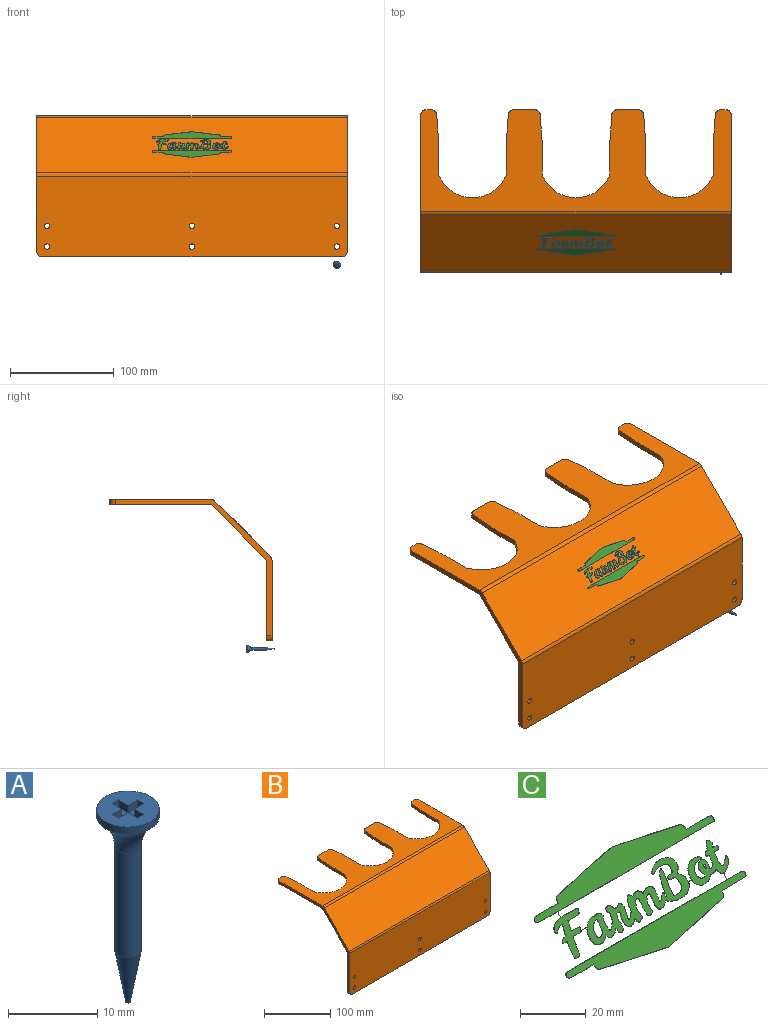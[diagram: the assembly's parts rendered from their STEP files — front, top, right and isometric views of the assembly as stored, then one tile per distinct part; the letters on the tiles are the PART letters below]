
ASSEMBLY  parts=3 mates=1
PART A: 19 faces, bbox 14.1x14.1x26.4 mm
  f0: plane 7x7mm, normal (0,0,1), area 31.5mm2, adj f3,f5,f6,f7,f8,f9,f10,f11
  f1: cylinder r=1.5mm len=14.31mm, axis (0,0,-1), area 134.9mm2, adj f4,f18
  f2: plane 0.5x0.5mm, normal (0,0,-1), area 0.2mm2, adj f18
  f3: cylinder r=3.5mm len=7mm, axis (0,0,-1), area 22mm2, adj f0,f4
  f4: torus R=6.5mm, axis (0,0,1), area 63.7mm2, adj f1,f3
  f5: plane 1.5x1mm, normal (0,1,0), area 1.5mm2, adj f0,f6,f16,f17
  f6: plane 1.5x1mm, normal (1,0,0), area 1.5mm2, adj f0,f5,f7,f17
  f7: plane 1x1mm, normal (0,1,0), area 1mm2, adj f0,f6,f8,f17
  f8: plane 1.5x1mm, normal (-1,0,0), area 1.5mm2, adj f0,f7,f9,f17
  f9: plane 1.5x1mm, normal (0,1,0), area 1.5mm2, adj f0,f8,f10,f17
  f10: plane 1x1mm, normal (-1,0,0), area 1mm2, adj f0,f9,f11,f17
  f11: plane 1.5x1mm, normal (0,-1,0), area 1.5mm2, adj f0,f10,f12,f17
  f12: plane 1.5x1mm, normal (-1,0,0), area 1.5mm2, adj f0,f11,f13,f17
  f13: plane 1x1mm, normal (0,-1,0), area 1mm2, adj f0,f12,f14,f17
  f14: plane 1.5x1mm, normal (1,0,0), area 1.5mm2, adj f0,f13,f15,f17
  f15: plane 1.5x1mm, normal (0,-1,0), area 1.5mm2, adj f0,f14,f16,f17
  f16: plane 1x1mm, normal (1,0,0), area 1mm2, adj f0,f5,f15,f17
  f17: plane 4x4mm, normal (0,0,1), area 7mm2, adj f5,f6,f7,f8,f9,f10,f11,f12
  f18: cone r=1.5mm half-angle=10deg, axis (0,0,1), area 39.6mm2, adj f1,f2
PART B: 52 faces, bbox 300x156.6x136.6 mm
  f0: plane 300x97.93mm, normal (0,0,-1), area 13697.5mm2, adj f1,f3,f4,f5,f6,f7,f8,f9
  f1: plane 5.36x5mm, normal (0,1,0), area 26.8mm2, adj f0,f2,f33,f44
  f2: plane 300x97.93mm, normal (0,0,1), area 13697.5mm2, adj f1,f3,f4,f5,f6,f7,f8,f9
  f3: plane 20.73x5mm, normal (0,1,0), area 103.6mm2, adj f0,f2,f24,f34
  f4: plane 20.73x5mm, normal (0,1,0), area 103.6mm2, adj f0,f2,f15,f25
  f5: plane 5.36x5mm, normal (0,1,0), area 26.8mm2, adj f0,f2,f16,f43
  f6: plane 151.57x131.57mm, normal (-1,0,0), area 1228.2mm2, adj f0,f2,f35,f36,f37,f38,f40,f41
  f7: plane 151.57x131.57mm, normal (1,0,0), area 1228.2mm2, adj f0,f2,f35,f36,f37,f38,f40,f42
  f8: plane 20.82x5mm, normal (-1,0.08,0), area 104.4mm2, adj f0,f2,f14,f15
  f9: plane 20.82x5mm, normal (1,0.08,0), area 104.4mm2, adj f0,f2,f13,f16
  f10: plane 22.43x5mm, normal (1,0,0), area 112.2mm2, adj f0,f2,f11,f13
  f11: cylinder r=35mm len=65mm, axis (0,0,1), area 416.7mm2, adj f0,f2,f10,f12
  f12: plane 22.43x5mm, normal (-1,0,0), area 112.2mm2, adj f0,f2,f11,f14
  f13: cylinder r=200mm len=15.11mm, axis (0,0,1), area 75.6mm2, adj f0,f2,f9,f10
  f14: cylinder r=200mm len=15.11mm, axis (0,0,1), area 75.6mm2, adj f0,f2,f8,f12
  f15: cylinder r=5mm len=5mm, axis (0,0,1), area 37.4mm2, adj f0,f2,f4,f8
  f16: cylinder r=5mm len=5mm, axis (0,0,-1), area 37.4mm2, adj f0,f2,f5,f9
  f17: plane 20.82x5mm, normal (-1,0.08,0), area 104.4mm2, adj f0,f2,f23,f24
  f18: plane 20.82x5mm, normal (1,0.08,0), area 104.4mm2, adj f0,f2,f22,f25
  f19: plane 22.43x5mm, normal (1,0,0), area 112.2mm2, adj f0,f2,f20,f22
  f20: cylinder r=35mm len=65mm, axis (0,0,1), area 416.7mm2, adj f0,f2,f19,f21
  f21: plane 22.43x5mm, normal (-1,0,0), area 112.2mm2, adj f0,f2,f20,f23
  f22: cylinder r=200mm len=15.11mm, axis (0,0,1), area 75.6mm2, adj f0,f2,f18,f19
  f23: cylinder r=200mm len=15.11mm, axis (0,0,1), area 75.6mm2, adj f0,f2,f17,f21
  f24: cylinder r=5mm len=5mm, axis (0,0,1), area 37.4mm2, adj f0,f2,f3,f17
  f25: cylinder r=5mm len=5mm, axis (0,0,-1), area 37.4mm2, adj f0,f2,f4,f18
  f26: plane 20.82x5mm, normal (-1,0.08,0), area 104.4mm2, adj f0,f2,f32,f33
  f27: plane 20.82x5mm, normal (1,0.08,0), area 104.4mm2, adj f0,f2,f31,f34
  f28: plane 22.43x5mm, normal (1,0,0), area 112.2mm2, adj f0,f2,f29,f31
  f29: cylinder r=35mm len=65mm, axis (0,0,1), area 416.7mm2, adj f0,f2,f28,f30
  f30: plane 22.43x5mm, normal (-1,0,0), area 112.2mm2, adj f0,f2,f29,f32
  f31: cylinder r=200mm len=15.11mm, axis (0,0,1), area 75.6mm2, adj f0,f2,f27,f28
  f32: cylinder r=200mm len=15.11mm, axis (0,0,1), area 75.6mm2, adj f0,f2,f26,f30
  f33: cylinder r=5mm len=5mm, axis (0,0,1), area 37.4mm2, adj f0,f1,f2,f26
  f34: cylinder r=5mm len=5mm, axis (0,0,-1), area 37.4mm2, adj f0,f2,f3,f27
  f35: plane 300x53.64mm, normal (0,0.71,-0.71), area 22757.4mm2, adj f0,f6,f7,f37
  f36: plane 300x53.64mm, normal (0,-0.71,0.71), area 22757.4mm2, adj f6,f7,f40,f45
  f37: plane 300x77.93mm, normal (0,1,0), area 23238.1mm2, adj f6,f7,f35,f39,f41,f42,f46,f47
  f38: plane 300x77.93mm, normal (0,-1,0), area 23238.1mm2, adj f6,f7,f39,f40,f41,f42,f46,f47
  f39: plane 290x5mm, normal (0,0,-1), area 1450mm2, adj f37,f38,f41,f42
  f40: cylinder r=5mm len=300mm, axis (1,0,0), area 1178.1mm2, adj f6,f7,f36,f38
  f41: cylinder r=5mm len=5mm, axis (0,1,0), area 39.3mm2, adj f6,f37,f38,f39
  f42: cylinder r=5mm len=5mm, axis (0,-1,0), area 39.3mm2, adj f7,f37,f38,f39
  f43: cylinder r=5mm len=5mm, axis (0,0,-1), area 39.3mm2, adj f0,f2,f5,f6
  f44: cylinder r=5mm len=5mm, axis (0,0,1), area 39.3mm2, adj f0,f1,f2,f7
  f45: cylinder r=5mm len=300mm, axis (1,0,0), area 1178.1mm2, adj f2,f6,f7,f36
  f46: cylinder r=2.62mm len=5.25mm, axis (0,-1,0), area 82.5mm2, adj f37,f38
  f47: cylinder r=2.62mm len=5.25mm, axis (0,-1,0), area 82.5mm2, adj f37,f38
  f48: cylinder r=2.62mm len=5.25mm, axis (0,-1,0), area 82.5mm2, adj f37,f38
  f49: cylinder r=2.62mm len=5.25mm, axis (0,-1,0), area 82.5mm2, adj f37,f38
  f50: cylinder r=2.62mm len=5.25mm, axis (0,-1,0), area 82.5mm2, adj f37,f38
  f51: cylinder r=2.62mm len=5.25mm, axis (0,-1,0), area 82.5mm2, adj f37,f38
PART C: 232 faces, bbox 77x24.9x24.9 mm
  f0: extruded ~0.63x0.63mm, area 0.1mm2, adj f1,f229,f230,f231
  f1: extruded ~0.72x0.72mm, area 0.1mm2, adj f0,f2,f230,f231
  f2: extruded ~0.56x0.56mm, area 0.1mm2, adj f1,f229,f230,f231
  f3: extruded ~1.22x0.3mm, area 0.1mm2, adj f4,f227,f230,f231
  f4: extruded ~0.97x0.97mm, area 0.1mm2, adj f3,f5,f230,f231
  f5: extruded ~2.07x2.07mm, area 0.3mm2, adj f4,f6,f230,f231
  f6: extruded ~1.87x0.7mm, area 0.2mm2, adj f5,f7,f230,f231
  f7: extruded ~0.65x0.65mm, area 0.1mm2, adj f6,f8,f230,f231
  f8: extruded ~1.21x1.21mm, area 0.2mm2, adj f7,f227,f230,f231
  f9: extruded ~6.37x0.14mm, area 0.6mm2, adj f10,f228,f230,f231
  f10: plane 1.72x1.72mm, normal (1,0,0), area 0.2mm2, adj f9,f11,f230,f231
  f11: extruded ~4.13x2.15mm, area 0.5mm2, adj f10,f12,f230,f231
  f12: extruded ~0.88x0.88mm, area 0.1mm2, adj f11,f13,f230,f231
  f13: extruded ~0.93x0.6mm, area 0.1mm2, adj f12,f14,f230,f231
  f14: extruded ~2.2x1mm, area 0.3mm2, adj f13,f15,f230,f231
  f15: extruded ~2.1x2.1mm, area 0.3mm2, adj f14,f16,f230,f231
  f16: extruded ~1.29x1.29mm, area 0.2mm2, adj f15,f17,f230,f231
  f17: extruded ~1.02x0.2mm, area 0.1mm2, adj f16,f18,f230,f231
  f18: extruded ~1.09x0.36mm, area 0.1mm2, adj f17,f19,f230,f231
  f19: extruded ~0.58x0.58mm, area 0.1mm2, adj f18,f20,f230,f231
  f20: extruded ~0.91x0.29mm, area 0.1mm2, adj f19,f21,f230,f231
  f21: extruded ~0.91x0.14mm, area 0.1mm2, adj f20,f22,f230,f231
  f22: extruded ~0.54x0.54mm, area 0.1mm2, adj f21,f23,f230,f231
  f23: plane 0.47x0.47mm, normal (0.87,-0.35,-0.35), area 0.1mm2, adj f22,f24,f230,f231
  f24: plane 0.48x0.48mm, normal (0.91,0.29,0.29), area 0.1mm2, adj f23,f25,f230,f231
  f25: extruded ~2.37x1.45mm, area 0.4mm2, adj f24,f26,f230,f231
  f26: extruded ~0.75x0.6mm, area 0.1mm2, adj f25,f27,f230,f231
  f27: extruded ~0.87x0.75mm, area 0.1mm2, adj f26,f28,f230,f231
  f28: extruded ~0.41x0.4mm, area 0.1mm2, adj f27,f29,f230,f231
  f29: extruded ~0.51x0.12mm, area 0.1mm2, adj f28,f30,f230,f231
  f30: extruded ~0.74x0.74mm, area 0.1mm2, adj f29,f31,f230,f231
  f31: extruded ~1.02x1.02mm, area 0.1mm2, adj f30,f32,f230,f231
  f32: extruded ~1.01x0.93mm, area 0.2mm2, adj f31,f33,f230,f231
  f33: extruded ~0.78x0.28mm, area 0.1mm2, adj f32,f34,f230,f231
  f34: extruded ~0.97x0.97mm, area 0.1mm2, adj f33,f35,f230,f231
  f35: extruded ~1.06x1.06mm, area 0.1mm2, adj f34,f36,f230,f231
  f36: extruded ~1.45x0.55mm, area 0.2mm2, adj f35,f37,f230,f231
  f37: extruded ~3.02x3.02mm, area 0.6mm2, adj f36,f38,f230,f231
  f38: plane 0.45x0.42mm, normal (-0.74,-0.47,-0.47), area 0.1mm2, adj f37,f39,f230,f231
  f39: plane 0.5x0.17mm, normal (-0.27,0.68,0.68), area 0.1mm2, adj f38,f40,f230,f231
  f40: extruded ~2.56x1.49mm, area 0.4mm2, adj f39,f41,f230,f231
  f41: extruded ~2.21x2.21mm, area 0.4mm2, adj f40,f42,f230,f231
  f42: extruded ~1.46x0.26mm, area 0.1mm2, adj f41,f43,f230,f231
  f43: extruded ~1.25x0.42mm, area 0.2mm2, adj f42,f44,f230,f231
  f44: extruded ~3.53x0.65mm, area 0.4mm2, adj f43,f45,f230,f231
  f45: extruded ~3.22x1.99mm, area 0.4mm2, adj f44,f46,f230,f231
  f46: extruded ~1.84x1.84mm, area 0.3mm2, adj f45,f47,f230,f231
  f47: plane 1.41x0.07mm, normal (0,0.71,0.71), area 0.1mm2, adj f46,f48,f230,f231
  f48: extruded ~1.6x1.6mm, area 0.2mm2, adj f47,f49,f230,f231
  f49: extruded ~1.57x1.22mm, area 0.2mm2, adj f48,f50,f230,f231
  f50: extruded ~0.6x0.55mm, area 0.1mm2, adj f49,f51,f230,f231
  f51: extruded ~2.23x2.23mm, area 0.3mm2, adj f50,f52,f230,f231
  f52: extruded ~2.13x1.57mm, area 0.3mm2, adj f51,f53,f230,f231
  f53: extruded ~4.3x0.34mm, area 0.4mm2, adj f52,f54,f230,f231
  f54: extruded ~3.31x1.78mm, area 0.4mm2, adj f53,f55,f230,f231
  f55: extruded ~1.5x0.37mm, area 0.2mm2, adj f54,f56,f230,f231
  f56: extruded ~3.3x0.58mm, area 0.3mm2, adj f55,f57,f230,f231
  f57: extruded ~2.29x1.48mm, area 0.3mm2, adj f56,f58,f230,f231
  f58: extruded ~0.9x0.9mm, area 0.1mm2, adj f57,f59,f230,f231
  f59: extruded ~1.22x0.4mm, area 0.1mm2, adj f58,f60,f230,f231
  f60: extruded ~1.26x0.32mm, area 0.1mm2, adj f59,f61,f230,f231
  f61: extruded ~0.46x0.46mm, area 0.1mm2, adj f60,f62,f230,f231
  f62: extruded ~1.49x0.53mm, area 0.2mm2, adj f61,f63,f230,f231
  f63: extruded ~1.17x0.41mm, area 0.1mm2, adj f62,f64,f230,f231
  f64: extruded ~2.13x2.13mm, area 0.3mm2, adj f63,f65,f230,f231
  f65: extruded ~2.6x1.08mm, area 0.3mm2, adj f64,f66,f230,f231
  f66: extruded ~1.62x0.27mm, area 0.2mm2, adj f65,f67,f230,f231
  f67: extruded ~3.46x3.46mm, area 0.5mm2, adj f66,f68,f230,f231
  f68: extruded ~2.97x2.97mm, area 0.5mm2, adj f67,f69,f230,f231
  f69: extruded ~4.75x4.75mm, area 0.7mm2, adj f68,f70,f230,f231
  f70: extruded ~0.83x0.83mm, area 0.1mm2, adj f69,f71,f230,f231
  f71: extruded ~0.61x0.61mm, area 0.1mm2, adj f70,f72,f230,f231
  f72: extruded ~0.68x0.68mm, area 0.1mm2, adj f71,f73,f230,f231
  f73: extruded ~1.24x0.75mm, area 0.2mm2, adj f72,f74,f230,f231
  f74: extruded ~1.5x0.81mm, area 0.2mm2, adj f73,f75,f230,f231
  f75: extruded ~1.15x1.15mm, area 0.2mm2, adj f74,f76,f230,f231
  f76: extruded ~2.26x2.26mm, area 0.3mm2, adj f75,f77,f230,f231
  f77: extruded ~0.6x0.51mm, area 0.1mm2, adj f76,f78,f230,f231
  f78: extruded ~3.28x0.68mm, area 0.4mm2, adj f77,f79,f230,f231
  f79: plane 0.34x0.3mm, normal (-0.69,0.51,0.51), area 0mm2, adj f78,f80,f230,f231
  f80: plane 0.32x0.32mm, normal (0.97,0.17,0.17), area 0mm2, adj f79,f81,f230,f231
  f81: extruded ~1.07x0.95mm, area 0.2mm2, adj f80,f82,f230,f231
  f82: extruded ~2.28x0.43mm, area 0.2mm2, adj f81,f83,f230,f231
  f83: extruded ~0.61x0.28mm, area 0.1mm2, adj f82,f84,f230,f231
  f84: extruded ~0.5x0.5mm, area 0.1mm2, adj f83,f85,f230,f231
  f85: extruded ~0.79x0.37mm, area 0.1mm2, adj f84,f86,f230,f231
  f86: extruded ~0.81x0.59mm, area 0.1mm2, adj f85,f87,f230,f231
  f87: extruded ~2.36x2.36mm, area 0.3mm2, adj f86,f88,f230,f231
  f88: plane 0.66x0.66mm, normal (-1,0.07,0.07), area 0.1mm2, adj f87,f89,f230,f231
  f89: plane 0.97x0.71mm, normal (-0.68,0.52,0.52), area 0.1mm2, adj f88,f90,f230,f231
  f90: extruded ~1.73x1.73mm, area 0.4mm2, adj f89,f91,f230,f231
  f91: plane 1.46x1.46mm, normal (0.96,-0.19,-0.19), area 0.2mm2, adj f90,f92,f230,f231
  f92: plane 0.5x0.5mm, normal (0.89,0.32,0.32), area 0.1mm2, adj f91,f93,f230,f231
  f93: extruded ~1.57x0.6mm, area 0.2mm2, adj f92,f94,f230,f231
  f94: extruded ~1.25x0.31mm, area 0.1mm2, adj f93,f95,f230,f231
  f95: extruded ~0.64x0.46mm, area 0.1mm2, adj f94,f96,f230,f231
  f96: extruded ~1.51x0.97mm, area 0.2mm2, adj f95,f97,f230,f231
  f97: extruded ~1.19x0.66mm, area 0.2mm2, adj f96,f98,f230,f231
  f98: extruded ~1x1mm, area 0.1mm2, adj f97,f99,f230,f231
  f99: extruded ~0.88x0.88mm, area 0.1mm2, adj f98,f100,f230,f231
  f100: extruded ~0.9x0.9mm, area 0.1mm2, adj f99,f101,f230,f231
  f101: extruded ~2.35x1.75mm, area 0.3mm2, adj f100,f102,f230,f231
  f102: extruded ~1.36x1.36mm, area 0.2mm2, adj f101,f103,f230,f231
  f103: extruded ~1.75x1.75mm, area 0.2mm2, adj f102,f104,f230,f231
  f104: plane 0.67x0.67mm, normal (0.9,-0.31,-0.31), area 0.1mm2, adj f103,f105,f230,f231
  f105: plane 0.39x0.39mm, normal (0.88,0.34,0.34), area 0.1mm2, adj f104,f106,f230,f231
  f106: extruded ~1.9x0.74mm, area 0.2mm2, adj f105,f107,f230,f231
  f107: extruded ~0.83x0.17mm, area 0.1mm2, adj f106,f108,f230,f231
  f108: extruded ~3.74x0.93mm, area 0.4mm2, adj f107,f109,f230,f231
  f109: extruded ~0.68x0.59mm, area 0.1mm2, adj f108,f110,f230,f231
  f110: plane 2.66x0.07mm, normal (0,0.71,0.71), area 0.3mm2, adj f109,f111,f230,f231
  f111: extruded ~0.91x0.91mm, area 0.1mm2, adj f110,f112,f230,f231
  f112: extruded ~1.71x0.2mm, area 0.2mm2, adj f111,f113,f230,f231
  f113: extruded ~1.58x0.23mm, area 0.2mm2, adj f112,f114,f230,f231
  f114: extruded ~1.2x1.2mm, area 0.2mm2, adj f113,f115,f230,f231
  f115: plane 1.06x1.06mm, normal (0.97,-0.17,-0.17), area 0.1mm2, adj f114,f116,f230,f231
  f116: plane 2.3x0.07mm, normal (0,-0.71,-0.71), area 0.2mm2, adj f115,f117,f230,f231
  f117: extruded ~3.04x0.78mm, area 0.4mm2, adj f116,f118,f230,f231
  f118: extruded ~3.07x0.77mm, area 0.4mm2, adj f117,f119,f230,f231
  f119: extruded ~4.14x0.13mm, area 0.4mm2, adj f118,f120,f230,f231
  f120: plane 1.5x1.5mm, normal (1,0,0), area 0.2mm2, adj f119,f121,f230,f231
  f121: extruded ~29.52x0.08mm, area 3mm2, adj f120,f122,f230,f231
  f122: plane 37.73x0.09mm, normal (0,-0.71,-0.71), area 3.8mm2, adj f121,f123,f230,f231
  f123: plane 0.29x0.29mm, normal (0.78,-0.44,-0.44), area 0mm2, adj f122,f124,f230,f231
  f124: extruded ~1x1mm, area 0.1mm2, adj f123,f125,f230,f231
  f125: extruded ~5.86x0.44mm, area 0.6mm2, adj f124,f126,f230,f231
  f126: plane 4.91x0.07mm, normal (0,0.71,0.71), area 0.5mm2, adj f125,f127,f230,f231
  f127: plane 0.53x0.53mm, normal (0.99,0.09,0.09), area 0.1mm2, adj f126,f128,f230,f231
  f128: extruded ~1.23x1.18mm, area 0.2mm2, adj f127,f129,f230,f231
  f129: extruded ~26.13x3.2mm, area 2.7mm2, adj f128,f130,f230,f231
  f130: extruded ~26.71x3.33mm, area 2.7mm2, adj f129,f131,f230,f231
  f131: extruded ~1.23x1.23mm, area 0.2mm2, adj f130,f132,f230,f231
  f132: plane 0.35x0.35mm, normal (-1,0,0), area 0mm2, adj f131,f133,f230,f231
  f133: plane 4.98x0.07mm, normal (0,0.71,0.71), area 0.5mm2, adj f132,f134,f230,f231
  f134: extruded ~5.43x0.23mm, area 0.5mm2, adj f133,f135,f230,f231
  f135: extruded ~1.36x1.36mm, area 0.2mm2, adj f134,f136,f230,f231
  f136: extruded ~8.52x0.16mm, area 0.9mm2, adj f135,f137,f230,f231
  f137: plane 1.5x1.5mm, normal (-1,0,0), area 0.2mm2, adj f136,f138,f230,f231
  f138: extruded ~1.91x0.32mm, area 0.2mm2, adj f137,f139,f230,f231
  f139: extruded ~2.71x1.78mm, area 0.4mm2, adj f138,f140,f230,f231
  f140: extruded ~1.13x0.65mm, area 0.2mm2, adj f139,f141,f230,f231
  f141: extruded ~2.24x0.85mm, area 0.3mm2, adj f140,f142,f230,f231
  f142: extruded ~0.51x0.21mm, area 0.1mm2, adj f141,f143,f230,f231
  f143: extruded ~1.35x1.35mm, area 0.2mm2, adj f142,f144,f230,f231
  f144: plane 1.17x1.17mm, normal (-0.94,0.24,0.24), area 0.2mm2, adj f143,f145,f230,f231
  f145: plane 0.76x0.28mm, normal (-0.36,0.66,0.66), area 0.1mm2, adj f144,f146,f230,f231
  f146: extruded ~1.49x0.94mm, area 0.2mm2, adj f145,f147,f230,f231
  f147: extruded ~0.92x0.24mm, area 0.1mm2, adj f146,f148,f230,f231
  f148: extruded ~0.86x0.26mm, area 0.1mm2, adj f147,f149,f230,f231
  f149: extruded ~3.92x3.92mm, area 0.6mm2, adj f148,f150,f230,f231
  f150: extruded ~1.96x0.27mm, area 0.2mm2, adj f149,f151,f230,f231
  f151: extruded ~0.85x0.85mm, area 0.1mm2, adj f150,f152,f230,f231
  f152: extruded ~2.71x2.71mm, area 0.4mm2, adj f151,f153,f230,f231
  f153: plane 0.89x0.89mm, normal (0.97,-0.16,-0.16), area 0.1mm2, adj f152,f154,f230,f231
  f154: plane 1.64x0.13mm, normal (-0.05,-0.71,-0.71), area 0.2mm2, adj f153,f155,f230,f231
  f155: extruded ~1.81x0.18mm, area 0.2mm2, adj f154,f156,f230,f231
  f156: extruded ~0.27x0.27mm, area 0mm2, adj f155,f157,f230,f231
  f157: plane 2.66x0.07mm, normal (0,-0.71,-0.71), area 0.3mm2, adj f156,f158,f230,f231
  f158: extruded ~2.39x2.39mm, area 0.4mm2, adj f157,f159,f230,f231
  f159: extruded ~1.69x1.69mm, area 0.2mm2, adj f158,f160,f230,f231
  f160: extruded ~4.82x0.87mm, area 0.5mm2, adj f159,f161,f230,f231
  f161: plane 0.39x0.39mm, normal (0.77,-0.45,-0.45), area 0.1mm2, adj f160,f162,f230,f231
  f162: plane 0.49x0.49mm, normal (-0.93,-0.25,-0.25), area 0.1mm2, adj f161,f163,f230,f231
  f163: extruded ~1.58x0.71mm, area 0.2mm2, adj f162,f164,f230,f231
  f164: extruded ~2.2x0.91mm, area 0.3mm2, adj f163,f165,f230,f231
  f165: plane 0.56x0.43mm, normal (0.68,-0.52,-0.52), area 0.1mm2, adj f164,f166,f230,f231
  f166: plane 0.55x0.55mm, normal (-0.99,-0.09,-0.09), area 0.1mm2, adj f165,f167,f230,f231
  f167: extruded ~0.97x0.97mm, area 0.2mm2, adj f166,f168,f230,f231
  f168: extruded ~1.35x0.52mm, area 0.2mm2, adj f167,f169,f230,f231
  f169: extruded ~1.24x1.24mm, area 0.2mm2, adj f168,f170,f230,f231
  f170: extruded ~1.77x1.77mm, area 0.2mm2, adj f169,f171,f230,f231
  f171: plane 0.76x0.76mm, normal (0.97,-0.17,-0.17), area 0.1mm2, adj f170,f172,f230,f231
  f172: plane 0.75x0.1mm, normal (0.05,-0.71,-0.71), area 0.1mm2, adj f171,f173,f230,f231
  f173: plane 0.75x0.1mm, normal (0.05,-0.71,-0.71), area 0.1mm2, adj f172,f174,f230,f231
  f174: plane 0.35x0.35mm, normal (-0.89,0.32,0.32), area 0mm2, adj f173,f175,f230,f231
  f175: extruded ~2.98x2.98mm, area 0.4mm2, adj f174,f176,f230,f231
  f176: extruded ~1.51x0.79mm, area 0.2mm2, adj f175,f177,f230,f231
  f177: extruded ~2.11x0.76mm, area 0.2mm2, adj f176,f178,f230,f231
  f178: plane 0.54x0.44mm, normal (0.69,-0.51,-0.51), area 0.1mm2, adj f177,f179,f230,f231
  f179: plane 0.52x0.52mm, normal (-0.99,-0.1,-0.1), area 0.1mm2, adj f178,f180,f230,f231
  f180: extruded ~1.78x0.83mm, area 0.3mm2, adj f179,f181,f230,f231
  f181: extruded ~1.22x1.22mm, area 0.2mm2, adj f180,f182,f230,f231
  f182: extruded ~2.13x2.13mm, area 0.3mm2, adj f181,f183,f230,f231
  f183: extruded ~1.53x1.31mm, area 0.2mm2, adj f182,f184,f230,f231
  f184: extruded ~1.54x1.54mm, area 0.2mm2, adj f183,f185,f230,f231
  f185: extruded ~3.02x3.02mm, area 0.4mm2, adj f184,f186,f230,f231
  f186: extruded ~1.82x0.37mm, area 0.2mm2, adj f185,f187,f230,f231
  f187: extruded ~0.71x0.71mm, area 0.1mm2, adj f186,f188,f230,f231
  f188: extruded ~0.92x0.92mm, area 0.1mm2, adj f187,f189,f230,f231
  f189: extruded ~1.87x1.87mm, area 0.3mm2, adj f188,f190,f230,f231
  f190: extruded ~1.33x0.75mm, area 0.2mm2, adj f189,f191,f230,f231
  f191: extruded ~1.63x1.63mm, area 0.2mm2, adj f190,f192,f230,f231
  f192: extruded ~2.62x2.62mm, area 0.5mm2, adj f191,f193,f230,f231
  f193: extruded ~1.85x0.76mm, area 0.2mm2, adj f192,f194,f230,f231
  f194: plane 0.5x0.39mm, normal (0.67,-0.52,-0.52), area 0.1mm2, adj f193,f195,f230,f231
  f195: plane 0.66x0.39mm, normal (-0.56,-0.59,-0.59), area 0.1mm2, adj f194,f196,f230,f231
  f196: extruded ~3.14x0.92mm, area 0.3mm2, adj f195,f197,f230,f231
  f197: extruded ~4.39x0.32mm, area 0.4mm2, adj f196,f198,f230,f231
  f198: extruded ~2.4x1.49mm, area 0.3mm2, adj f197,f199,f230,f231
  f199: extruded ~0.76x0.76mm, area 0.1mm2, adj f198,f200,f230,f231
  f200: plane 1.41x0.07mm, normal (0,-0.71,-0.71), area 0.1mm2, adj f199,f201,f230,f231
  f201: extruded ~0.73x0.73mm, area 0.1mm2, adj f200,f202,f230,f231
  f202: extruded ~2.22x1.53mm, area 0.3mm2, adj f201,f203,f230,f231
  f203: extruded ~1.43x0.13mm, area 0.1mm2, adj f202,f204,f230,f231
  f204: extruded ~2.77x0.81mm, area 0.3mm2, adj f203,f205,f230,f231
  f205: extruded ~1.43x0.37mm, area 0.2mm2, adj f204,f206,f230,f231
  f206: extruded ~1.43x0.27mm, area 0.1mm2, adj f205,f207,f230,f231
  f207: extruded ~0.69x0.43mm, area 0.1mm2, adj f206,f208,f230,f231
  f208: extruded ~1.09x1.03mm, area 0.2mm2, adj f207,f209,f230,f231
  f209: extruded ~0.4x0.11mm, area 0mm2, adj f208,f210,f230,f231
  f210: plane 1.72x1.72mm, normal (-1,0,0), area 0.2mm2, adj f209,f211,f230,f231
  f211: extruded ~31.4x0.1mm, area 3.1mm2, adj f210,f212,f230,f231
  f212: extruded ~37.82x0.23mm, area 3.8mm2, adj f211,f213,f230,f231
  f213: extruded ~0.99x0.99mm, area 0.2mm2, adj f212,f214,f230,f231
  f214: extruded ~5.85x0.56mm, area 0.6mm2, adj f213,f215,f230,f231
  f215: plane 5.03x0.07mm, normal (0,-0.71,-0.71), area 0.5mm2, adj f214,f216,f230,f231
  f216: plane 0.53x0.53mm, normal (-0.99,-0.08,-0.08), area 0.1mm2, adj f215,f217,f230,f231
  f217: extruded ~1.05x1.05mm, area 0.2mm2, adj f216,f218,f230,f231
  f218: extruded ~12.8x1.72mm, area 1.3mm2, adj f217,f219,f230,f231
  f219: extruded ~13.12x1.67mm, area 1.3mm2, adj f218,f220,f230,f231
  f220: extruded ~0.65x0.17mm, area 0.1mm2, adj f219,f221,f230,f231
  f221: extruded ~26.53x3.34mm, area 2.7mm2, adj f220,f222,f230,f231
  f222: extruded ~1.15x1.15mm, area 0.2mm2, adj f221,f223,f230,f231
  f223: plane 0.45x0.45mm, normal (1,-0.03,-0.03), area 0.1mm2, adj f222,f224,f230,f231
  f224: plane 10.5x0.16mm, normal (0.01,-0.71,-0.71), area 1.1mm2, adj f223,f225,f230,f231
  f225: plane 0.29x0.29mm, normal (0.78,-0.44,-0.44), area 0mm2, adj f224,f226,f230,f231
  f226: extruded ~1x1mm, area 0.1mm2, adj f225,f228,f230,f231
  f227: extruded ~2x2mm, area 0.3mm2, adj f3,f8,f230,f231
  f228: extruded ~0.54x0.34mm, area 0.1mm2, adj f9,f226,f230,f231
  f229: extruded ~0.61x0.61mm, area 0.1mm2, adj f0,f2,f230,f231
  f230: plane 77.01x24.78mm, normal (0,-0.71,0.71), area 1191.9mm2, adj f0,f1,f2,f3,f4,f5,f6,f7
  f231: plane 77.01x24.78mm, normal (0,0.71,-0.71), area 1191.9mm2, adj f0,f1,f2,f3,f4,f5,f6,f7
PLACE A rot(axis=(-1,0,0),90deg) t=(140.08,-126.54,-121.89)mm
PLACE B t=(0.08,-18,17.36)mm
PLACE C t=(0,-17.68,17.68)mm
MATE fastened B.f36 <-> C.f231  axis (0,-0.71,0.71) through (0.08,-96.28,-5.92)mm
